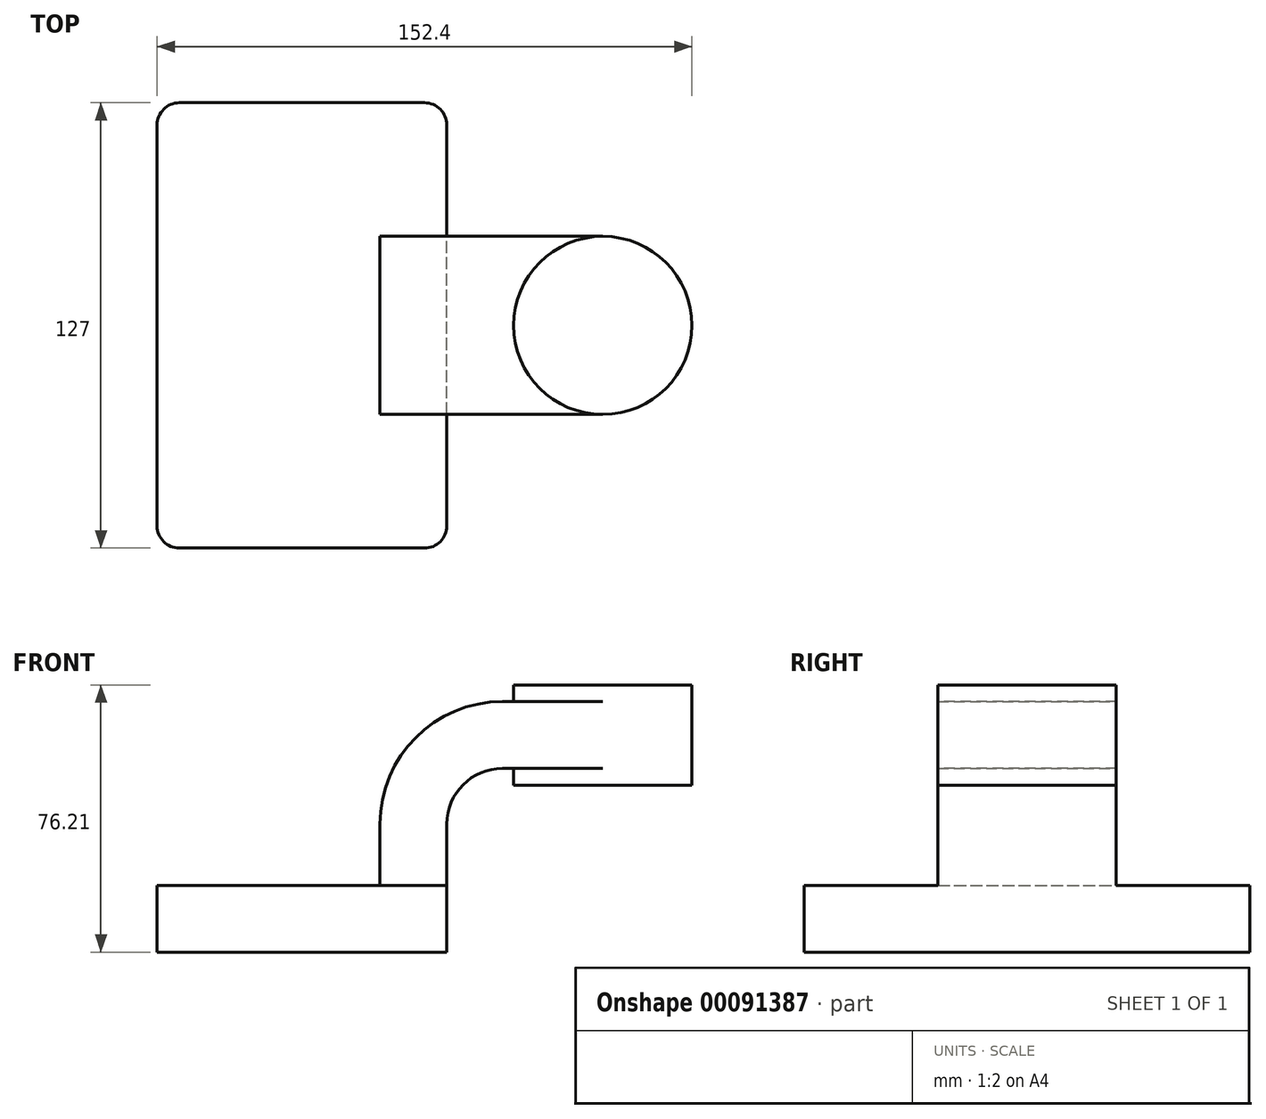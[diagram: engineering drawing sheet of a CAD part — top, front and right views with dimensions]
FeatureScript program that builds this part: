
annotation { "Feature Type Name" : "Feature", "Feature Type Description" : "" }
export const myFeature = defineFeature(function(context is Context, id is Id, definition is map)
    precondition{}
    {
        {
            var Q0;
            Q0=qCreatedBy(makeId("Front.planeOp"),FACE);
            var sketch = newSketch(context, id + "F0", { "sketchPlane" : qUnion([Q0])});
            skLineSegment(sketch, "E0.bottom", {"start": v(41.27, 9.53) * mm, "end": v(-41.28, 9.53) * mm});
            skLineSegment(sketch, "E0.top", {"start": v(41.28, -9.52) * mm, "end": v(-41.27, -9.52) * mm});
            skLineSegment(sketch, "E0.left", {"start": v(41.28, 9.53) * mm, "end": v(41.28, -9.52) * mm});
            skLineSegment(sketch, "E0.right", {"start": v(-41.28, 9.53) * mm, "end": v(-41.27, -9.52) * mm});
            skPoint(sketch, "E0.middle", {"position": v(0, 0) * mm});
            skLineSegment(sketch, "E1.bottom", {"start": v(111.13, 38.1) * mm, "end": v(60.33, 38.1) * mm});
            skLineSegment(sketch, "E1.top", {"start": v(111.13, 66.68) * mm, "end": v(60.33, 66.68) * mm});
            skLineSegment(sketch, "E1.left", {"start": v(111.13, 38.1) * mm, "end": v(111.13, 66.68) * mm});
            skLineSegment(sketch, "E1.right", {"start": v(60.33, 38.1) * mm, "end": v(60.33, 66.68) * mm});
            skPoint(sketch, "E1.middle", {"position": v(85.73, 52.39) * mm});
            skLineSegment(sketch, "E2", {"start": v(41.27, 9.53) * mm, "end": v(41.27, 26.99) * mm});
            skArc(sketch, "E3", {"start": v(41.27, 26.99) * mm, "mid": v(45.92, 38.21) * mm, "end": v(57.15, 42.86) * mm});
            skLineSegment(sketch, "E4", {"start": v(57.15, 42.86) * mm, "end": v(85.72, 42.86) * mm});
            skLineSegment(sketch, "E5.0", {"start": v(57.15, 61.91) * mm, "end": v(85.72, 61.91) * mm});
            skArc(sketch, "E5.1", {"start": v(22.23, 26.99) * mm, "mid": v(32.45, 51.68) * mm, "end": v(57.15, 61.91) * mm});
            skLineSegment(sketch, "E5.2", {"start": v(22.23, 9.53) * mm, "end": v(22.23, 26.99) * mm});
            skFitSpline(sketch, "E6", {"points": [v(-41.28, 9.53) * mm, v(57.15, 61.91) * mm], "startDerivative": vector(4.22, 63.92) * mm, "endDerivative": vector(220.04, 0.04) * mm});
            skLineSegment(sketch, "E7", {"start": v(85.73, 66.68) * mm, "end": v(85.73, 38.1) * mm});
            skSolve(sketch);
        }
        {
            var Q0;
            Q0=makeQuery(id+"F0.imprint","IMPRINT",FACE,{"disambiguationData":[TD([[makeQuery(id+"F0.imprint","IMPRINT",EDGE,{"derivedFrom":sQuery(id+"F0.wireOp",EDGE,"E0.top")}),-1.0]])]});
            extrude(context, id + "F1", {"entities" : qUnion([Q0]), "endBound" : BoundingType.SYMMETRIC, "depth" : 127 * mm});
        }
        {
            var Q0;
            {var subQ1=sQuery(id+"F0.wireOp",EDGE,"E2");Q0=makeQuery(id+"F0.imprint","IMPRINT",FACE,{"disambiguationData":[TD([[makeQuery(id+"F0.imprint","IMPRINT",EDGE,{"derivedFrom":subQ1}),1.0]])]});}
            var Q1;
            {var subQ0=sQuery(id+"F0.wireOp",EDGE,"E4");var subQ1=sQuery(id+"F0.wireOp",EDGE,"E1.right");var subQ2=makeQuery(id+"F0.imprint","INTERSECT",VERTEX,{"derivedFrom":[subQ1,subQ0]});Q1=makeQuery(id+"F0.imprint","IMPRINT",FACE,{"disambiguationData":[TD([[makeQuery(id+"F0.imprint","IMPRINT",EDGE,{"disambiguationData":[TD([[subQ2,-1.0]])],"derivedFrom":subQ1}),-1.0]])]});}
            extrude(context, id + "F2", {"entities" : qUnion([Q0, Q1]), "operationType" : NewBodyOperationType.ADD, "endBound" : BoundingType.SYMMETRIC, "depth" : 50.8 * mm});
        }
        {
            var Q0;
            Q0=makeQuery(id+"F0.imprint","IMPRINT",FACE,{"disambiguationData":[TD([[makeQuery(id+"F0.imprint","IMPRINT",EDGE,{"derivedFrom":sQuery(id+"F0.wireOp",EDGE,"E5.1")}),1.0]])]});
            extrude(context, id + "F3", {"entities" : qUnion([Q0]), "operationType" : NewBodyOperationType.ADD, "endBound" : BoundingType.SYMMETRIC, "depth" : 15.88 * mm});
        }
        {
            var Q0;
            {var subQ0=sQuery(id+"F0.wireOp",EDGE,"E1.left");Q0=makeQuery(id+"F0.imprint","IMPRINT",FACE,{"disambiguationData":[TD([[makeQuery(id+"F0.imprint","IMPRINT",EDGE,{"derivedFrom":subQ0}),1.0]])]});}
            var Q1;
            Q1=sQuery(id+"F0.wireOp",EDGE,"E7");
            revolve(context, id + "F4", {"operationType" : NewBodyOperationType.ADD, "entities" : qUnion([Q0]), "axis" : qUnion([Q1]), "revolveType" : RevolveType.FULL});
        }
        {
            var Q0;
            Q0=makeQuery(id+"F1.opExtrude","CAP_EDGE",EDGE,{"disambiguationData":[OSD([sQuery(id+"F0.wireOp",EDGE,"E0.left")])],"isStart":false});
            var Q1;
            Q1=makeQuery(id+"F1.opExtrude","CAP_EDGE",EDGE,{"disambiguationData":[OSD([sQuery(id+"F0.wireOp",EDGE,"E0.right")])],"isStart":false});
            var Q2;
            Q2=makeQuery(id+"F1.opExtrude","CAP_EDGE",EDGE,{"disambiguationData":[OSD([sQuery(id+"F0.wireOp",EDGE,"E0.left")])],"isStart":true});
            var Q3;
            Q3=makeQuery(id+"F1.opExtrude","CAP_EDGE",EDGE,{"disambiguationData":[OSD([sQuery(id+"F0.wireOp",EDGE,"E0.right")])],"isStart":true});
            fillet(context, id + "F5", {"entities" : qUnion([Q0, Q1, Q2, Q3]), "radius" : 6.35 * mm, "tangentPropagation" : true, "allowEdgeOverflow" : false});
        }
    });
